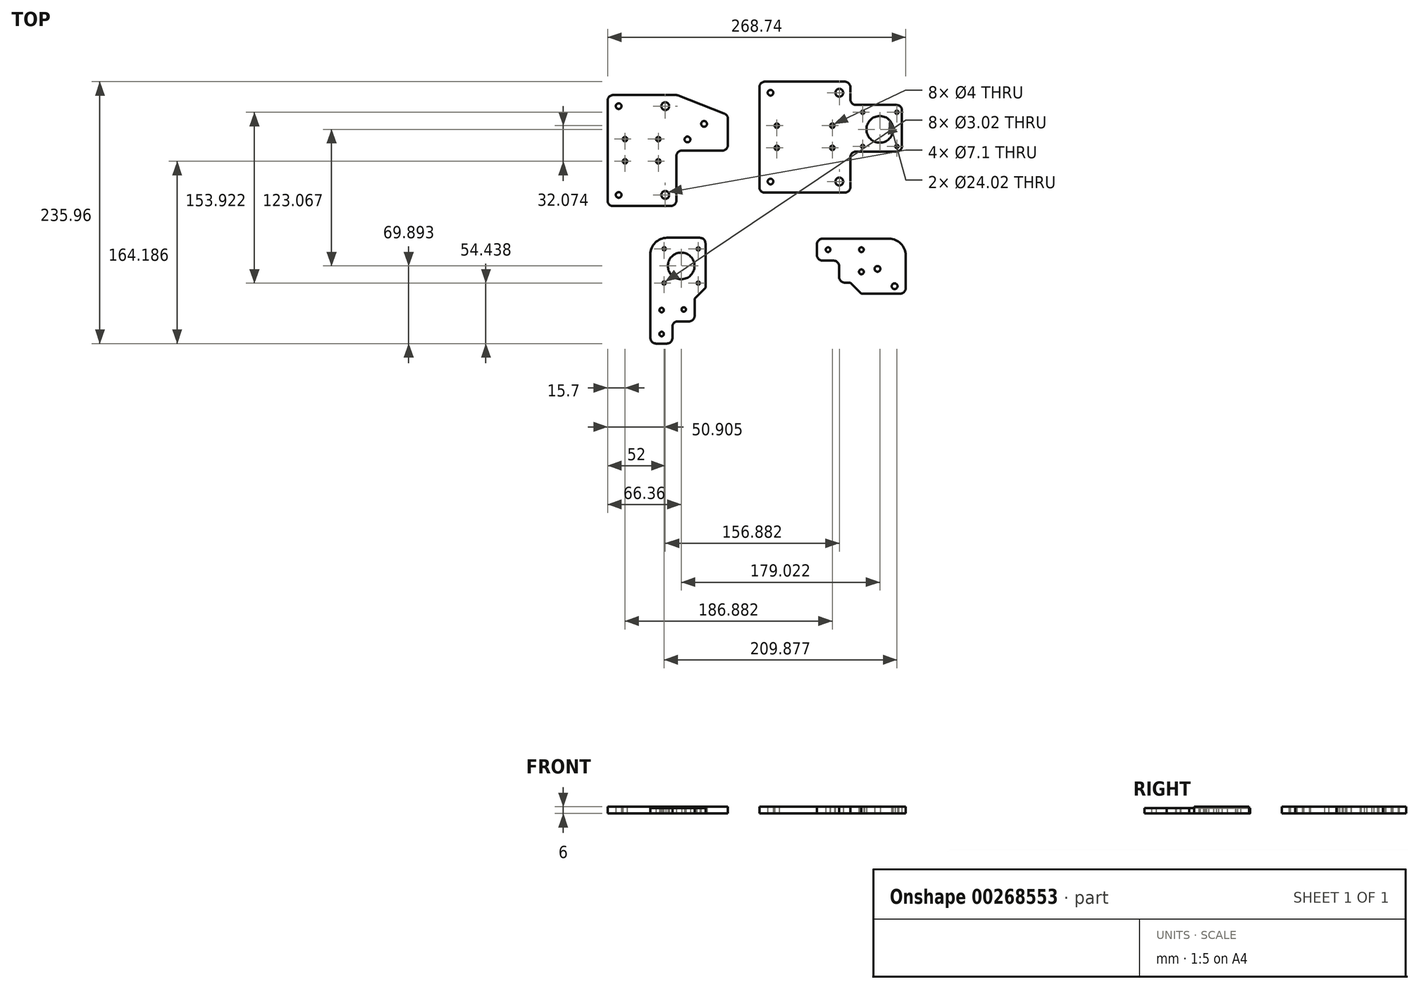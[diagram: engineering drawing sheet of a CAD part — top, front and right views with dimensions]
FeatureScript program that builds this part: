
annotation { "Feature Type Name" : "Feature", "Feature Type Description" : "" }
export const myFeature = defineFeature(function(context is Context, id is Id, definition is map)
    precondition{}
    {
        {
            var Q0;
            Q0=qCreatedBy(makeId("Top.planeOp"),FACE);
            var sketch = newSketch(context, id + "F0", { "sketchPlane" : qUnion([Q0])});
            skLineSegment(sketch, "E0", {"start": v(-27.76, 55) * mm, "end": v(-27.76, -40.26) * mm});
            skLineSegment(sketch, "E1", {"start": v(-27.76, -40.26) * mm, "end": v(-7.91, -40.26) * mm});
            skLineSegment(sketch, "E2", {"start": v(-7.91, -40.26) * mm, "end": v(-7.91, -20.34) * mm});
            skLineSegment(sketch, "E3", {"start": v(-7.91, -20.34) * mm, "end": v(12.1, -20.34) * mm});
            skLineSegment(sketch, "E4", {"start": v(12.1, -20.34) * mm, "end": v(12.1, 0) * mm});
            skLineSegment(sketch, "E5", {"start": v(12.1, 0) * mm, "end": v(21.88, 0) * mm});
            skLineSegment(sketch, "E6", {"start": v(21.88, 0) * mm, "end": v(21.88, 55) * mm});
            skLineSegment(sketch, "E7", {"start": v(21.88, 55) * mm, "end": v(-27.76, 55) * mm});
            skCircle(sketch, "E8", {"center": v(0, 29.63) * mm, "radius": 12 * mm});
            skCircle(sketch, "E9", {"center": v(-15.34, 45.09) * mm, "radius": 1.51 * mm});
            skCircle(sketch, "E10", {"center": v(-17.64, -10.14) * mm, "radius": 2.01 * mm});
            skCircle(sketch, "E11", {"center": v(2.3, -9.57) * mm, "radius": 2.01 * mm});
            skCircle(sketch, "E12", {"center": v(-17.64, -31.7) * mm, "radius": 2.01 * mm});
            skCircle(sketch, "E13.1.0", {"center": v(-15.45, 14.29) * mm, "radius": 1.51 * mm});
            skCircle(sketch, "E13.2.0", {"center": v(15.34, 14.18) * mm, "radius": 1.51 * mm});
            skCircle(sketch, "E13.3.0", {"center": v(15.45, 44.98) * mm, "radius": 1.51 * mm});
            skSolve(sketch);
        }
        {
            var Q0;
            Q0=makeQuery(id+"F0.imprint","IMPRINT",FACE,{"disambiguationData":[TD([[makeQuery(id+"F0.imprint","IMPRINT",EDGE,{"derivedFrom":sQuery(id+"F0.wireOp",EDGE,"E0")}),1.0]])]});
            extrude(context, id + "F1", {"entities" : qUnion([Q0]), "depth" : 5 * mm});
        }
        {
            var Q0;
            Q0=makeQuery(id+"F1.opExtrude","SWEPT_EDGE",EDGE,{"disambiguationData":[OSD([sQuery(id+"F0.wireOp",EDGE,"E0"),sQuery(id+"F0.wireOp",EDGE,"E7")])]});
            fillet(context, id + "F2", {"entities" : qUnion([Q0]), "radius" : 15 * mm, "tangentPropagation" : true, "allowEdgeOverflow" : false});
        }
        {
            var Q0;
            Q0=makeQuery(id+"F1.opExtrude","SWEPT_EDGE",EDGE,{"disambiguationData":[OSD([sQuery(id+"F0.wireOp",EDGE,"E6"),sQuery(id+"F0.wireOp",EDGE,"E7")])]});
            var Q1;
            Q1=makeQuery(id+"F1.opExtrude","SWEPT_EDGE",EDGE,{"disambiguationData":[OSD([sQuery(id+"F0.wireOp",EDGE,"E2"),sQuery(id+"F0.wireOp",EDGE,"E3")])]});
            var Q2;
            Q2=makeQuery(id+"F1.opExtrude","SWEPT_EDGE",EDGE,{"disambiguationData":[OSD([sQuery(id+"F0.wireOp",EDGE,"E1"),sQuery(id+"F0.wireOp",EDGE,"E2")])]});
            var Q3;
            Q3=makeQuery(id+"F1.opExtrude","SWEPT_EDGE",EDGE,{"disambiguationData":[OSD([sQuery(id+"F0.wireOp",EDGE,"E0"),sQuery(id+"F0.wireOp",EDGE,"E1")])]});
            var Q4;
            Q4=makeQuery(id+"F1.opExtrude","SWEPT_EDGE",EDGE,{"disambiguationData":[OSD([sQuery(id+"F0.wireOp",EDGE,"E3"),sQuery(id+"F0.wireOp",EDGE,"E4")])]});
            fillet(context, id + "F3", {"entities" : qUnion([Q0, Q1, Q2, Q3, Q4]), "radius" : 5 * mm, "tangentPropagation" : true, "allowEdgeOverflow" : false});
        }
        {
            var Q0;
            Q0=makeQuery(id+"F1.opExtrude","SWEPT_EDGE",EDGE,{"disambiguationData":[OSD([sQuery(id+"F0.wireOp",EDGE,"E5"),sQuery(id+"F0.wireOp",EDGE,"E6")])]});
            chamfer(context, id + "F4", {"entities" : qUnion([Q0]), "width" : 10 * mm, "tangentPropagation" : true});
        }
        {
            var Q0;
            Q0=qCreatedBy(makeId("Top.planeOp"),FACE);
            var sketch = newSketch(context, id + "F5", { "sketchPlane" : qUnion([Q0])});
            skLineSegment(sketch, "E14", {"start": v(70.52, 59.7) * mm, "end": v(152.52, 59.7) * mm});
            skLineSegment(sketch, "E15", {"start": v(152.52, 59.7) * mm, "end": v(152.52, 38.7) * mm});
            skLineSegment(sketch, "E16", {"start": v(152.52, 38.7) * mm, "end": v(199.02, 38.7) * mm});
            skLineSegment(sketch, "E17", {"start": v(199.02, 38.7) * mm, "end": v(199.02, -3.3) * mm});
            skLineSegment(sketch, "E18", {"start": v(199.02, -3.3) * mm, "end": v(152.52, -3.3) * mm});
            skLineSegment(sketch, "E19", {"start": v(152.52, -3.3) * mm, "end": v(152.52, -40.3) * mm});
            skLineSegment(sketch, "E20", {"start": v(152.52, -40.3) * mm, "end": v(70.52, -40.3) * mm});
            skLineSegment(sketch, "E21", {"start": v(70.52, -40.3) * mm, "end": v(70.52, 59.7) * mm});
            skCircle(sketch, "E22", {"center": v(179.02, 16.7) * mm, "radius": 12 * mm});
            skCircle(sketch, "E23", {"center": v(163.62, 32.1) * mm, "radius": 1.51 * mm});
            skCircle(sketch, "E24.1.0", {"center": v(163.62, 1.3) * mm, "radius": 1.51 * mm});
            skCircle(sketch, "E24.2.0", {"center": v(194.42, 1.3) * mm, "radius": 1.51 * mm});
            skCircle(sketch, "E24.3.0", {"center": v(194.42, 32.1) * mm, "radius": 1.51 * mm});
            skCircle(sketch, "E25", {"center": v(142.52, -30.3) * mm, "radius": 3.55 * mm});
            skLineSegment(sketch, "E26", {"start": v(111.52, 64.43) * mm, "end": v(111.52, -53.16) * mm, "construction": true});
            skLineSegment(sketch, "E27", {"start": v(70.52, 9.7) * mm, "end": v(217.27, 9.7) * mm, "construction": true});
            skCircle(sketch, "E28.MirrorC", {"center": v(142.52, 49.7) * mm, "radius": 3.55 * mm});
            skCircle(sketch, "E29", {"center": v(80.52, -30.3) * mm, "radius": 2.55 * mm});
            skCircle(sketch, "E30.MirrorC", {"center": v(80.52, 49.7) * mm, "radius": 2.55 * mm});
            skCircle(sketch, "E31", {"center": v(86.22, 0) * mm, "radius": 2 * mm});
            skCircle(sketch, "E32.0.1.0", {"center": v(86.22, 20) * mm, "radius": 2 * mm});
            skCircle(sketch, "E32.1.0.0", {"center": v(136.22, 0) * mm, "radius": 2 * mm});
            skCircle(sketch, "E32.1.1.0", {"center": v(136.22, 20) * mm, "radius": 2 * mm});
            skLineSegment(sketch, "E32.direction1", {"start": v(86.22, 0) * mm, "end": v(136.22, 0) * mm, "construction": true});
            skLineSegment(sketch, "E32.direction2", {"start": v(86.22, 0) * mm, "end": v(86.22, 20) * mm, "construction": true});
            skSolve(sketch);
        }
        {
            var Q0;
            Q0=makeQuery(id+"F5.imprint","IMPRINT",FACE,{"disambiguationData":[TD([[makeQuery(id+"F5.imprint","IMPRINT",EDGE,{"derivedFrom":sQuery(id+"F5.wireOp",EDGE,"E14")}),-1.0]])]});
            extrude(context, id + "F6", {"entities" : qUnion([Q0]), "depth" : 6 * mm});
        }
        {
            var Q0;
            Q0=makeQuery(id+"F6.opExtrude","SWEPT_EDGE",EDGE,{"disambiguationData":[OSD([sQuery(id+"F5.wireOp",EDGE,"E20"),sQuery(id+"F5.wireOp",EDGE,"E21")])]});
            var Q1;
            Q1=makeQuery(id+"F6.opExtrude","SWEPT_EDGE",EDGE,{"disambiguationData":[OSD([sQuery(id+"F5.wireOp",EDGE,"E19"),sQuery(id+"F5.wireOp",EDGE,"E20")])]});
            var Q2;
            Q2=makeQuery(id+"F6.opExtrude","SWEPT_EDGE",EDGE,{"disambiguationData":[OSD([sQuery(id+"F5.wireOp",EDGE,"E17"),sQuery(id+"F5.wireOp",EDGE,"E18")])]});
            var Q3;
            Q3=makeQuery(id+"F6.opExtrude","SWEPT_EDGE",EDGE,{"disambiguationData":[OSD([sQuery(id+"F5.wireOp",EDGE,"E18"),sQuery(id+"F5.wireOp",EDGE,"E19")])]});
            var Q4;
            Q4=makeQuery(id+"F6.opExtrude","SWEPT_EDGE",EDGE,{"disambiguationData":[OSD([sQuery(id+"F5.wireOp",EDGE,"E14"),sQuery(id+"F5.wireOp",EDGE,"E21")])]});
            var Q5;
            Q5=makeQuery(id+"F6.opExtrude","SWEPT_EDGE",EDGE,{"disambiguationData":[OSD([sQuery(id+"F5.wireOp",EDGE,"E14"),sQuery(id+"F5.wireOp",EDGE,"E15")])]});
            var Q6;
            Q6=makeQuery(id+"F6.opExtrude","SWEPT_EDGE",EDGE,{"disambiguationData":[OSD([sQuery(id+"F5.wireOp",EDGE,"E15"),sQuery(id+"F5.wireOp",EDGE,"E16")])]});
            var Q7;
            Q7=makeQuery(id+"F6.opExtrude","SWEPT_EDGE",EDGE,{"disambiguationData":[OSD([sQuery(id+"F5.wireOp",EDGE,"E16"),sQuery(id+"F5.wireOp",EDGE,"E17")])]});
            fillet(context, id + "F7", {"entities" : qUnion([Q0, Q1, Q2, Q3, Q4, Q5, Q6, Q7]), "radius" : 5 * mm, "tangentPropagation" : true, "allowEdgeOverflow" : false});
        }
        {
            var Q0;
            Q0=makeQuery(id+"F1.opExtrude","SWEPT_BODY",BODY,{"disambiguationData":[OSD([sQuery(id+"F0.wireOp",EDGE,"E0"),sQuery(id+"F0.wireOp",EDGE,"E1"),sQuery(id+"F0.wireOp",EDGE,"E2"),sQuery(id+"F0.wireOp",EDGE,"E3"),sQuery(id+"F0.wireOp",EDGE,"E4"),sQuery(id+"F0.wireOp",EDGE,"E5"),sQuery(id+"F0.wireOp",EDGE,"E6"),sQuery(id+"F0.wireOp",EDGE,"E7"),sQuery(id+"F0.wireOp",EDGE,"E8"),sQuery(id+"F0.wireOp",EDGE,"E9"),sQuery(id+"F0.wireOp",EDGE,"E10"),sQuery(id+"F0.wireOp",EDGE,"E11"),sQuery(id+"F0.wireOp",EDGE,"E12"),sQuery(id+"F0.wireOp",EDGE,"E13.1.0"),sQuery(id+"F0.wireOp",EDGE,"E13.2.0"),sQuery(id+"F0.wireOp",EDGE,"E13.3.0")])]});
            transform(context, id + "F8", {"entities" : qUnion([Q0]), "transformType" : TransformType.TRANSLATION_3D, "dx" : 0 * mm, "dy" : -136 * mm, "dz" : 0 * mm, "makeCopy" : false});
        }
        {
            var Q0;
            Q0=qCreatedBy(makeId("Top.planeOp"),FACE);
            var sketch = newSketch(context, id + "F9", { "sketchPlane" : qUnion([Q0])});
            skLineSegment(sketch, "E33", {"start": v(-66.36, 47.63) * mm, "end": v(-4.36, 47.63) * mm});
            skLineSegment(sketch, "E34", {"start": v(-4.36, 47.8) * mm, "end": v(-4.36, 47.63) * mm});
            skLineSegment(sketch, "E35", {"start": v(42.14, 29.63) * mm, "end": v(42.14, -2.37) * mm});
            skLineSegment(sketch, "E36", {"start": v(42.14, -2.37) * mm, "end": v(-4.36, -2.37) * mm});
            skLineSegment(sketch, "E37", {"start": v(-4.36, -2.37) * mm, "end": v(-4.36, -52.37) * mm});
            skLineSegment(sketch, "E38", {"start": v(-4.36, -52.37) * mm, "end": v(-66.36, -52.37) * mm});
            skLineSegment(sketch, "E39", {"start": v(-66.36, -52.37) * mm, "end": v(-66.36, 47.63) * mm});
            skCircle(sketch, "E40", {"center": v(-14.36, -42.37) * mm, "radius": 3.55 * mm});
            skLineSegment(sketch, "E41", {"start": v(-35.36, 52.36) * mm, "end": v(-35.36, -65.24) * mm, "construction": true});
            skLineSegment(sketch, "E42", {"start": v(-66.36, -2.37) * mm, "end": v(80.08, -2.37) * mm, "construction": true});
            skCircle(sketch, "E43.MirrorC", {"center": v(-14.36, 37.63) * mm, "radius": 3.55 * mm});
            skCircle(sketch, "E44", {"center": v(-56.36, -42.37) * mm, "radius": 2.55 * mm});
            skCircle(sketch, "E45.MirrorC", {"center": v(-56.36, 37.63) * mm, "radius": 2.55 * mm});
            skCircle(sketch, "E46", {"center": v(-50.66, -12.07) * mm, "radius": 2 * mm});
            skCircle(sketch, "E47.0.1.0", {"center": v(-50.66, 7.93) * mm, "radius": 2 * mm});
            skCircle(sketch, "E47.1.0.0", {"center": v(-20.66, -12.07) * mm, "radius": 2 * mm});
            skCircle(sketch, "E47.1.1.0", {"center": v(-20.66, 7.93) * mm, "radius": 2 * mm});
            skLineSegment(sketch, "E47.direction1", {"start": v(-50.66, -12.07) * mm, "end": v(-20.66, -12.07) * mm, "construction": true});
            skLineSegment(sketch, "E47.direction2", {"start": v(-50.66, -12.07) * mm, "end": v(-50.66, 7.93) * mm, "construction": true});
            skLineSegment(sketch, "E48", {"start": v(-4.36, 47.8) * mm, "end": v(42.14, 29.63) * mm});
            skLineSegment(sketch, "E49", {"start": v(-4.36, -2.37) * mm, "end": v(-4.36, 47.8) * mm, "construction": true});
            skCircle(sketch, "E50", {"center": v(5.64, 7.63) * mm, "radius": 2.6 * mm});
            skCircle(sketch, "E51", {"center": v(20.64, 21.63) * mm, "radius": 2.6 * mm});
            skSolve(sketch);
        }
        {
            var Q0;
            Q0=makeQuery(id+"F9.imprint","IMPRINT",FACE,{"disambiguationData":[TD([[makeQuery(id+"F9.imprint","IMPRINT",EDGE,{"derivedFrom":sQuery(id+"F9.wireOp",EDGE,"E33")}),-1.0]])]});
            extrude(context, id + "F10", {"entities" : qUnion([Q0]), "depth" : 6 * mm});
        }
        {
            var Q0;
            Q0=makeQuery(id+"F10.opExtrude","SWEPT_EDGE",EDGE,{"disambiguationData":[OSD([sQuery(id+"F9.wireOp",EDGE,"E34"),sQuery(id+"F9.wireOp",EDGE,"E48")])]});
            var Q1;
            Q1=makeQuery(id+"F10.opExtrude","SWEPT_EDGE",EDGE,{"disambiguationData":[OSD([sQuery(id+"F9.wireOp",EDGE,"E35"),sQuery(id+"F9.wireOp",EDGE,"E48")])]});
            var Q2;
            Q2=makeQuery(id+"F10.opExtrude","SWEPT_EDGE",EDGE,{"disambiguationData":[OSD([sQuery(id+"F9.wireOp",EDGE,"E35"),sQuery(id+"F9.wireOp",EDGE,"E36")])]});
            var Q3;
            Q3=makeQuery(id+"F10.opExtrude","SWEPT_EDGE",EDGE,{"disambiguationData":[OSD([sQuery(id+"F9.wireOp",EDGE,"E36"),sQuery(id+"F9.wireOp",EDGE,"E37")])]});
            var Q4;
            Q4=makeQuery(id+"F10.opExtrude","SWEPT_EDGE",EDGE,{"disambiguationData":[OSD([sQuery(id+"F9.wireOp",EDGE,"E37"),sQuery(id+"F9.wireOp",EDGE,"E38")])]});
            var Q5;
            Q5=makeQuery(id+"F10.opExtrude","SWEPT_EDGE",EDGE,{"disambiguationData":[OSD([sQuery(id+"F9.wireOp",EDGE,"E38"),sQuery(id+"F9.wireOp",EDGE,"E39")])]});
            var Q6;
            Q6=makeQuery(id+"F10.opExtrude","SWEPT_EDGE",EDGE,{"disambiguationData":[OSD([sQuery(id+"F9.wireOp",EDGE,"E33"),sQuery(id+"F9.wireOp",EDGE,"E39")])]});
            fillet(context, id + "F11", {"entities" : qUnion([Q0, Q1, Q2, Q3, Q4, Q5, Q6]), "radius" : 5 * mm, "tangentPropagation" : true, "allowEdgeOverflow" : false});
        }
        {
            var Q0;
            Q0=qCreatedBy(makeId("Top.planeOp"),FACE);
            var sketch = newSketch(context, id + "F12", { "sketchPlane" : qUnion([Q0])});
            skLineSegment(sketch, "E52", {"start": v(202.38, -81.82) * mm, "end": v(122.38, -81.82) * mm});
            skLineSegment(sketch, "E53", {"start": v(122.38, -81.82) * mm, "end": v(122.38, -101.56) * mm});
            skLineSegment(sketch, "E54", {"start": v(142.38, -101.56) * mm, "end": v(122.38, -101.56) * mm});
            skLineSegment(sketch, "E55", {"start": v(142.38, -101.56) * mm, "end": v(142.38, -121.39) * mm});
            skLineSegment(sketch, "E56", {"start": v(162.45, -121.39) * mm, "end": v(142.38, -121.39) * mm});
            skLineSegment(sketch, "E57", {"start": v(162.45, -121.39) * mm, "end": v(162.45, -131.39) * mm});
            skLineSegment(sketch, "E58", {"start": v(162.45, -131.39) * mm, "end": v(202.38, -131.39) * mm});
            skLineSegment(sketch, "E59", {"start": v(202.38, -131.39) * mm, "end": v(202.38, -81.82) * mm});
            skCircle(sketch, "E60", {"center": v(132.43, -91.69) * mm, "radius": 2.12 * mm});
            skPoint(sketch, "E60.centerSnap0", {"position": v(122.38, -91.69) * mm});
            skCircle(sketch, "E61", {"center": v(162.43, -91.69) * mm, "radius": 2.12 * mm});
            skCircle(sketch, "E62", {"center": v(162.45, -111.69) * mm, "radius": 2.17 * mm});
            skLineSegment(sketch, "E63", {"start": v(162.43, -79.74) * mm, "end": v(162.45, -129.84) * mm, "construction": true});
            skCircle(sketch, "E64", {"center": v(176.96, -109) * mm, "radius": 2.58 * mm});
            skCircle(sketch, "E65", {"center": v(192.38, -124.64) * mm, "radius": 2.58 * mm});
            skSolve(sketch);
        }
        {
            var Q0;
            Q0=makeQuery(id+"F12.imprint","IMPRINT",FACE,{"disambiguationData":[TD([[makeQuery(id+"F12.imprint","IMPRINT",EDGE,{"derivedFrom":sQuery(id+"F12.wireOp",EDGE,"E52")}),1.0]])]});
            extrude(context, id + "F13", {"entities" : qUnion([Q0]), "depth" : 6 * mm});
        }
        {
            var Q0;
            Q0=makeQuery(id+"F13.opExtrude","SWEPT_EDGE",EDGE,{"disambiguationData":[OSD([sQuery(id+"F12.wireOp",EDGE,"E52"),sQuery(id+"F12.wireOp",EDGE,"E53")])]});
            var Q1;
            Q1=makeQuery(id+"F13.opExtrude","SWEPT_EDGE",EDGE,{"disambiguationData":[OSD([sQuery(id+"F12.wireOp",EDGE,"E53"),sQuery(id+"F12.wireOp",EDGE,"E54")])]});
            var Q2;
            Q2=makeQuery(id+"F13.opExtrude","SWEPT_EDGE",EDGE,{"disambiguationData":[OSD([sQuery(id+"F12.wireOp",EDGE,"E54"),sQuery(id+"F12.wireOp",EDGE,"E55")])]});
            var Q3;
            Q3=makeQuery(id+"F13.opExtrude","SWEPT_EDGE",EDGE,{"disambiguationData":[OSD([sQuery(id+"F12.wireOp",EDGE,"E55"),sQuery(id+"F12.wireOp",EDGE,"E56")])]});
            var Q4;
            Q4=makeQuery(id+"F13.opExtrude","SWEPT_EDGE",EDGE,{"disambiguationData":[OSD([sQuery(id+"F12.wireOp",EDGE,"E58"),sQuery(id+"F12.wireOp",EDGE,"E59")])]});
            fillet(context, id + "F14", {"entities" : qUnion([Q0, Q1, Q2, Q3, Q4]), "radius" : 5 * mm, "tangentPropagation" : true, "allowEdgeOverflow" : false});
        }
        {
            var Q0;
            Q0=makeQuery(id+"F13.opExtrude","SWEPT_EDGE",EDGE,{"disambiguationData":[OSD([sQuery(id+"F12.wireOp",EDGE,"E56"),sQuery(id+"F12.wireOp",EDGE,"E57")])]});
            chamfer(context, id + "F15", {"entities" : qUnion([Q0]), "width" : 10 * mm, "tangentPropagation" : true});
        }
        {
            var Q0;
            Q0=makeQuery(id+"F13.opExtrude","SWEPT_EDGE",EDGE,{"disambiguationData":[OSD([sQuery(id+"F12.wireOp",EDGE,"E52"),sQuery(id+"F12.wireOp",EDGE,"E59")])]});
            fillet(context, id + "F16", {"entities" : qUnion([Q0]), "radius" : 15 * mm, "tangentPropagation" : true, "allowEdgeOverflow" : false});
        }
    });
